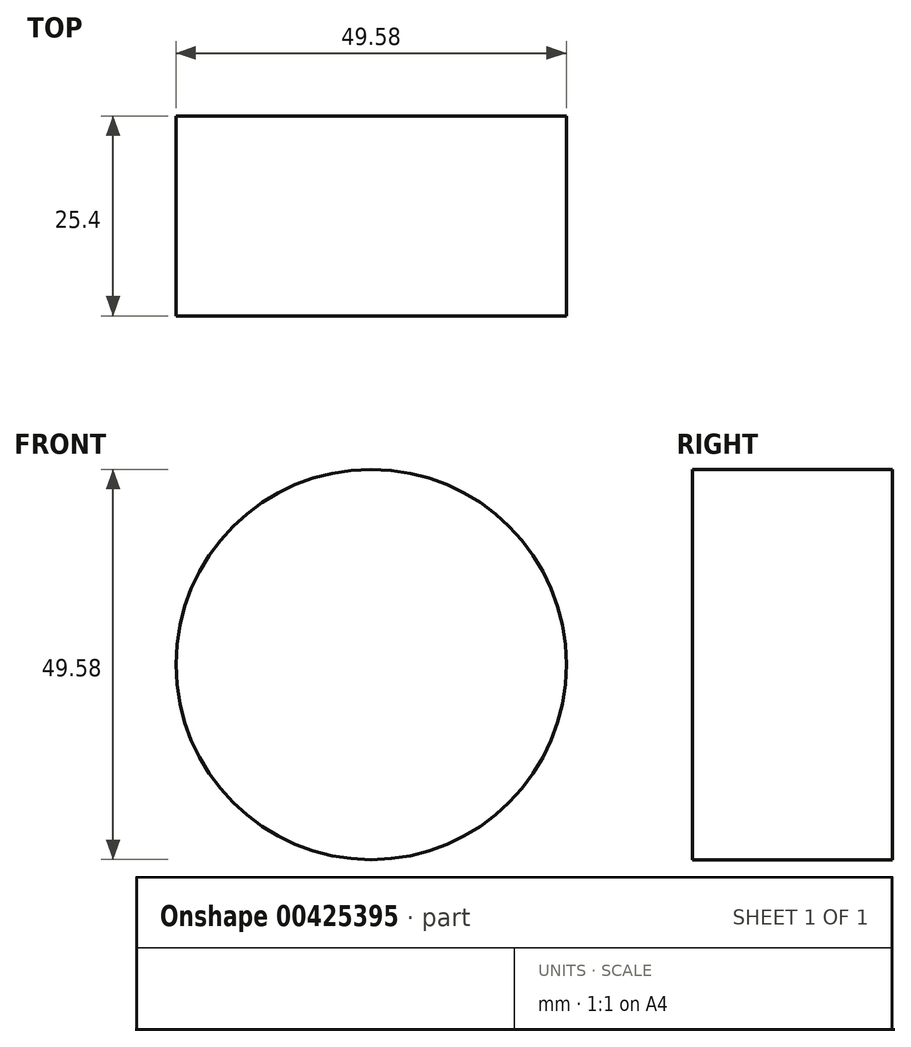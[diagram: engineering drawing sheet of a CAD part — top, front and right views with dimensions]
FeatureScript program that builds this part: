
annotation { "Feature Type Name" : "Feature", "Feature Type Description" : "" }
export const myFeature = defineFeature(function(context is Context, id is Id, definition is map)
    precondition{}
    {
        {
            var Q0;
            Q0=qCreatedBy(makeId("Front.planeOp"),FACE);
            var sketch = newSketch(context, id + "F0", { "sketchPlane" : qUnion([Q0])});
            skCircle(sketch, "E0", {"center": v(0, 0) * mm, "radius": 24.8 * mm});
            skSolve(sketch);
        }
        {
            var Q0;
            Q0=makeQuery(id+"F0.imprint","IMPRINT",FACE,{"disambiguationData":[TD([[makeQuery(id+"F0.imprint","IMPRINT",EDGE,{"derivedFrom":sQuery(id+"F0.wireOp",EDGE,"E0")}),1.0]])]});
            extrude(context, id + "F1", {"entities" : qUnion([Q0]), "depth" : 25.4 * mm});
        }
    });
